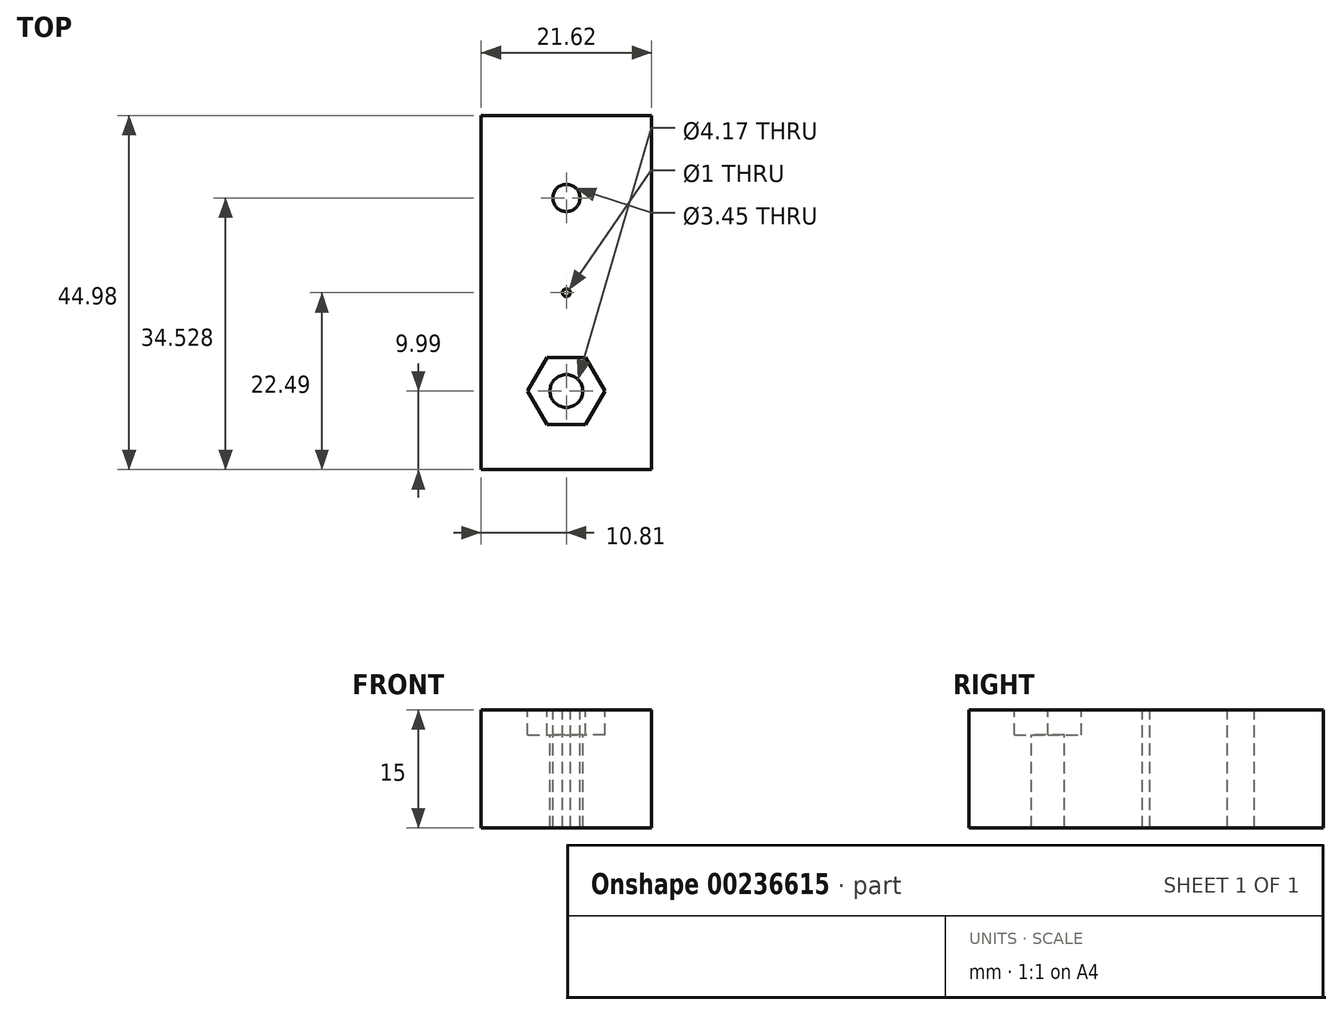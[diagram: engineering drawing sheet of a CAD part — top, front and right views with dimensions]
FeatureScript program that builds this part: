
annotation { "Feature Type Name" : "Feature", "Feature Type Description" : "" }
export const myFeature = defineFeature(function(context is Context, id is Id, definition is map)
    precondition{}
    {
        {
            var Q0;
            Q0=qCreatedBy(makeId("Top.planeOp"),FACE);
            var sketch = newSketch(context, id + "F0", { "sketchPlane" : qUnion([Q0])});
            skLineSegment(sketch, "E0.bottom", {"start": v(10.81, -22.5) * mm, "end": v(-10.81, -22.5) * mm});
            skLineSegment(sketch, "E0.top", {"start": v(10.81, 22.5) * mm, "end": v(-10.81, 22.5) * mm});
            skLineSegment(sketch, "E0.left", {"start": v(10.81, -22.5) * mm, "end": v(10.81, 22.5) * mm});
            skLineSegment(sketch, "E0.right", {"start": v(-10.81, -22.5) * mm, "end": v(-10.81, 22.5) * mm});
            skCircle(sketch, "E1", {"center": v(0, 12.04) * mm, "radius": 1.73 * mm});
            skCircle(sketch, "E2", {"center": v(0, -12.5) * mm, "radius": 2.08 * mm});
            skCircle(sketch, "E3", {"center": v(0, 0) * mm, "radius": 0.5 * mm});
            skCircle(sketch, "E4.cCircle", {"center": v(0, -12.5) * mm, "radius": 4.25 * mm, "construction": true});
            skLineSegment(sketch, "E4.0", {"start": v(-2.45, -8.25) * mm, "end": v(2.45, -8.25) * mm});
            skLineSegment(sketch, "E4.1", {"start": v(2.45, -8.25) * mm, "end": v(4.9, -12.5) * mm});
            skLineSegment(sketch, "E4.2", {"start": v(4.9, -12.5) * mm, "end": v(2.45, -16.75) * mm});
            skLineSegment(sketch, "E4.3", {"start": v(2.45, -16.75) * mm, "end": v(-2.45, -16.75) * mm});
            skLineSegment(sketch, "E4.4", {"start": v(-2.45, -16.75) * mm, "end": v(-4.9, -12.5) * mm});
            skLineSegment(sketch, "E4.5", {"start": v(-4.9, -12.5) * mm, "end": v(-2.45, -8.25) * mm});
            skPoint(sketch, "E4.0.midPoint", {"position": v(0, -8.25) * mm});
            skSolve(sketch);
        }
        {
            var Q0;
            Q0=makeQuery(id+"F0.imprint","IMPRINT",FACE,{"disambiguationData":[TD([[makeQuery(id+"F0.imprint","IMPRINT",EDGE,{"derivedFrom":sQuery(id+"F0.wireOp",EDGE,"E0.bottom")}),-1.0]])]});
            var Q1;
            Q1=makeQuery(id+"F0.imprint","IMPRINT",FACE,{"disambiguationData":[TD([[makeQuery(id+"F0.imprint","IMPRINT",EDGE,{"derivedFrom":sQuery(id+"F0.wireOp",EDGE,"xmmMVhjA-I2DV-eg2p-HMhs-kmHElxxjFZvg")}),1.0]])]});
            var Q2;
            Q2=makeQuery(id+"F0.imprint","IMPRINT",FACE,{"disambiguationData":[TD([[makeQuery(id+"F0.imprint","IMPRINT",EDGE,{"derivedFrom":sQuery(id+"F0.wireOp",EDGE,"E2")}),-1.0]])]});
            extrude(context, id + "F1", {"entities" : qUnion([Q0, Q1, Q2]), "oppositeDirection" : true, "depth" : 15 * mm});
        }
        {
            var Q0;
            Q0=makeQuery(id+"F0.imprint","IMPRINT",FACE,{"disambiguationData":[TD([[makeQuery(id+"F0.imprint","IMPRINT",EDGE,{"derivedFrom":sQuery(id+"F0.wireOp",EDGE,"E2")}),-1.0]])]});
            extrude(context, id + "F2", {"entities" : qUnion([Q0]), "operationType" : NewBodyOperationType.REMOVE, "oppositeDirection" : true, "depth" : 3.2 * mm});
        }
    });
